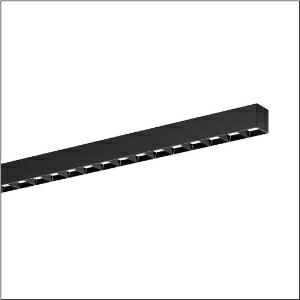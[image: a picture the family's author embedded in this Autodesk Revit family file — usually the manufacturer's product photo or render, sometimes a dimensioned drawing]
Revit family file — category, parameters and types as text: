
# Revit family: silica_r__21_51mx24dc4abb_c2b6
name_source: partatom
category: Lighting Fixtures
units: mm (PartAtom-declared; Revit-internal decimal feet)

## family parameters
Cut with Voids When Loaded = No
Host = Face
Light Source = No
Part Type = Normal
Room Calculation Point = No
Round Connector Dimension = Use Diameter
Shared = No

## types (1)
- --- (1 x LED, 10800 lm, 73.7 W, 4000K)
    Apparent Load = 74 VA
    CIE Flux Codes = 74 94 99 100 100
    Color Rendering = 80
    Color Temperature = 4000K
    Default Elevation = 1800 mm
    Description = Silica® 21, office luminaire, primary light control with darklight reflector, of PMMA, black, CAT 2 (L<= 3000cd/m²), light emission: direct distribution, primary light characteristic: asymmetric, installation type: surface-mounted, LED, rated luminous flux: 10.800lm, luminous efficacy: 147lm/W, light colour: 840, colour temperature: 4000K, with terminal, 3+2-pole, max. 2.5mm², mains connection: 220..240V, AC, 50/60Hz, rated input power: 73.7W, luminaire housing, of aluminium, jet black (RAL 9005), length: 3.004mm, width: 53mm, height: 53mm, protection rating (complete): IP20, insulation class (complete): insulation class I (protective earthing), certification: CE, permissible operating ambient temperature: 0..+35°C, standard: EN 50419, packaging unit: 1 piece
    Height = 0 mm  [stored 0 ft]
    Lamp = 1 x LED
    Lamp Light Flux = 10800 lm
    Lamp Power = 73.7 W
    Lamp count = 1
    Length = 3004 mm
    Luminous efficacy = 147 lm/W
    Manufacturer = Siteco
    ModVariant = No
    Model = 51MX24DC4ABB
    Mounting Place = Ceiling
    Mounting Type = Recessed
    Number of Poles = 1
    OnlyDefault = Yes
    Power Factor = 1
    Product Name = Silica® 21
    Product group = office luminaire | ceiling recessed
    ProductGroupID = 400
    Protection Class = Protection class I
    Protection Degree = IP 20
    RLX_Detail_Level = 1
    RLX_Emergency_Light_Flux = 0 lm
    RLX_Emergency_Type = 0
    RLX_Emergency_Type_DB = No
    RlxData = <blob elided: 64545 chars, md5=fdf2ef6f>
    Socket = socket
    Standby Power = 0 W
    System Light Flux = 10800 lm
    System Power = 74 W
    Type Comments = factory setting: luminous flux: 100 % | dim-lin: 254 | 418 mA
    Type Image = l_1335908.jpg
    URL = http://relux.com
    VarID = @adj_092369
    Voltage = 0 V
    Weight = 0.00 kg
    Width = 53 mm

note: [stored X ft] marks values corroborated as IEEE doubles in the binary element streams (Revit-internal decimal feet)

## geometry (parser evidence)
native form markers: Blend x4, Sweep x9
no freeform markers — native parametric forms only
